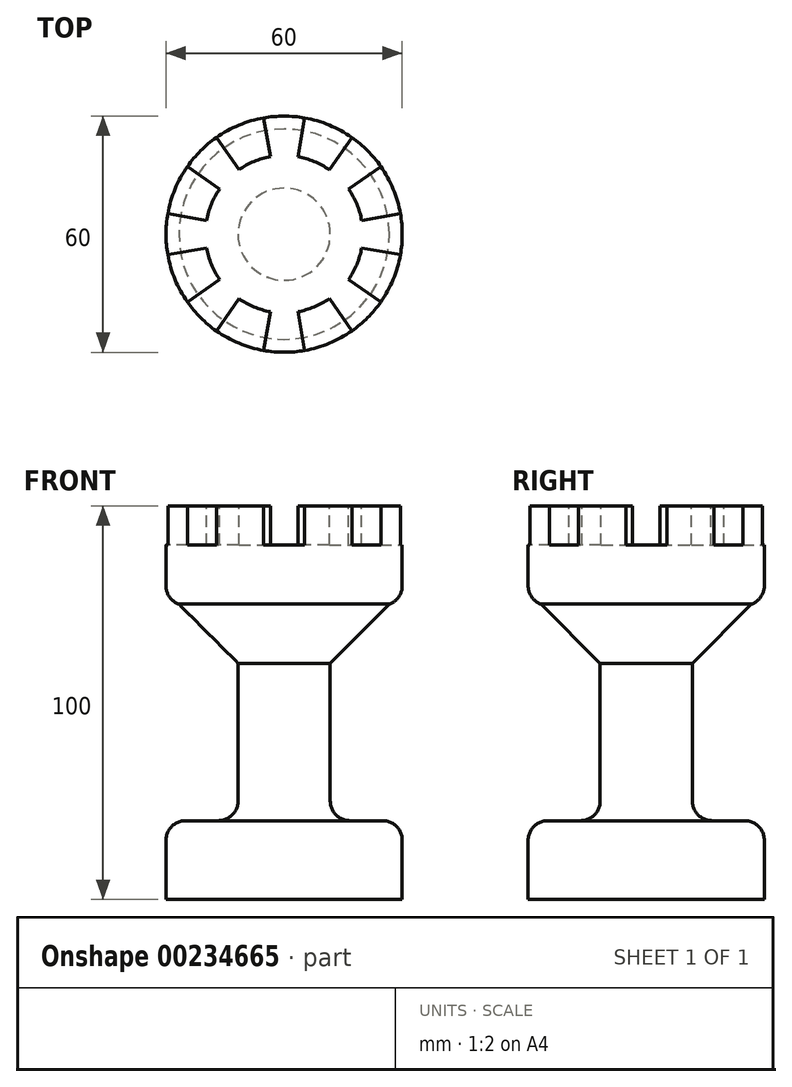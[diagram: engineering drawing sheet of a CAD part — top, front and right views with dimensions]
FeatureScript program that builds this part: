
annotation { "Feature Type Name" : "Feature", "Feature Type Description" : "" }
export const myFeature = defineFeature(function(context is Context, id is Id, definition is map)
    precondition{}
    {
        {
            var Q0;
            Q0=qCreatedBy(makeId("Front.planeOp"),FACE);
            var sketch = newSketch(context, id + "F0", { "sketchPlane" : qUnion([Q0])});
            skLineSegment(sketch, "E0.bottom", {"start": v(0, 0) * mm, "end": v(-30, 0) * mm});
            skLineSegment(sketch, "E0.top", {"start": v(-11.71, 20) * mm, "end": v(-30, 20) * mm});
            skLineSegment(sketch, "E0.right", {"start": v(-30, 0) * mm, "end": v(-30, 20) * mm});
            skLineSegment(sketch, "E1.left", {"start": v(-11.71, 75) * mm, "end": v(-11.71, 20) * mm});
            skLineSegment(sketch, "E2.bottom", {"start": v(-30, 100) * mm, "end": v(-20, 100) * mm});
            skLineSegment(sketch, "E2.top", {"start": v(-30, 75) * mm, "end": v(-11.71, 75) * mm});
            skLineSegment(sketch, "E2.left", {"start": v(-30, 100) * mm, "end": v(-30, 75) * mm});
            skLineSegment(sketch, "E3.top", {"start": v(-20, 90) * mm, "end": v(0, 90) * mm});
            skLineSegment(sketch, "E3.left", {"start": v(-20, 100) * mm, "end": v(-20, 90) * mm});
            skPoint(sketch, "E0.left.end.orphan", {"position": v(0, 20) * mm});
            skPoint(sketch, "E0.left.start.orphan", {"position": v(0, 10) * mm});
            skLineSegment(sketch, "E4", {"start": v(0, 90) * mm, "end": v(0, 0) * mm});
            skSolve(sketch);
        }
        {
            var Q0;
            Q0 = qSketchRegion(id + "F0", true);
            var Q1;
            Q1=sQuery(id+"F0.wireOp",EDGE,"E4");
            revolve(context, id + "F1", {"entities" : qUnion([Q0]), "axis" : qUnion([Q1]), "revolveType" : RevolveType.FULL});
        }
        {
            var Q0;
            Q0=makeQuery(id+"F1.opRevolve","SWEPT_FACE",FACE,{"disambiguationData":[OSD([sQuery(id+"F0.wireOp",EDGE,"E2.bottom")])]});
            var sketch = newSketch(context, id + "F2", { "sketchPlane" : qUnion([Q0])});
            skLineSegment(sketch, "E5", {"start": v(3.25, 18.43) * mm, "end": v(5.56, 31.52) * mm});
            skLineSegment(sketch, "E6", {"start": v(-3.25, 18.43) * mm, "end": v(-5.56, 31.52) * mm});
            skPoint(sketch, "E7.end.orphan", {"position": v(0, 37.14) * mm});
            skArc(sketch, "E8", {"start": v(3.25, 18.43) * mm, "mid": v(0, 18.71) * mm, "end": v(-3.25, 18.43) * mm});
            skArc(sketch, "E9", {"start": v(5.56, 31.52) * mm, "mid": v(0, 32) * mm, "end": v(-5.56, 31.52) * mm});
            skPoint(sketch, "E10.orphan", {"position": v(-6.55, 37.14) * mm});
            skPoint(sketch, "E11.orphan", {"position": v(6.55, 37.14) * mm});
            skLineSegment(sketch, "E12.1.0", {"start": v(-10.73, 15.33) * mm, "end": v(-18.36, 26.22) * mm});
            skLineSegment(sketch, "E12.1.1", {"start": v(-15.33, 10.73) * mm, "end": v(-26.22, 18.36) * mm});
            skArc(sketch, "E12.1.2", {"start": v(-18.36, 26.22) * mm, "mid": v(-22.63, 22.63) * mm, "end": v(-26.22, 18.36) * mm});
            skArc(sketch, "E12.1.3", {"start": v(-10.73, 15.33) * mm, "mid": v(-13.23, 13.23) * mm, "end": v(-15.33, 10.73) * mm});
            skLineSegment(sketch, "E12.2.0", {"start": v(-18.43, 3.25) * mm, "end": v(-31.52, 5.56) * mm});
            skLineSegment(sketch, "E12.2.1", {"start": v(-18.43, -3.25) * mm, "end": v(-31.52, -5.56) * mm});
            skArc(sketch, "E12.2.2", {"start": v(-31.52, 5.56) * mm, "mid": v(-32, 0) * mm, "end": v(-31.52, -5.56) * mm});
            skArc(sketch, "E12.2.3", {"start": v(-18.43, 3.25) * mm, "mid": v(-18.71, 0) * mm, "end": v(-18.43, -3.25) * mm});
            skLineSegment(sketch, "E12.3.0", {"start": v(-15.33, -10.73) * mm, "end": v(-26.22, -18.36) * mm});
            skLineSegment(sketch, "E12.3.1", {"start": v(-10.73, -15.33) * mm, "end": v(-18.36, -26.22) * mm});
            skArc(sketch, "E12.3.2", {"start": v(-26.22, -18.36) * mm, "mid": v(-22.63, -22.63) * mm, "end": v(-18.36, -26.22) * mm});
            skArc(sketch, "E12.3.3", {"start": v(-15.33, -10.73) * mm, "mid": v(-13.23, -13.23) * mm, "end": v(-10.73, -15.33) * mm});
            skLineSegment(sketch, "E12.4.0", {"start": v(-3.25, -18.43) * mm, "end": v(-5.56, -31.52) * mm});
            skLineSegment(sketch, "E12.4.1", {"start": v(3.25, -18.43) * mm, "end": v(5.56, -31.52) * mm});
            skArc(sketch, "E12.4.2", {"start": v(-5.56, -31.52) * mm, "mid": v(0, -32) * mm, "end": v(5.56, -31.52) * mm});
            skArc(sketch, "E12.4.3", {"start": v(-3.25, -18.43) * mm, "mid": v(0, -18.71) * mm, "end": v(3.25, -18.43) * mm});
            skLineSegment(sketch, "E12.5.0", {"start": v(10.73, -15.33) * mm, "end": v(18.36, -26.22) * mm});
            skLineSegment(sketch, "E12.5.1", {"start": v(15.33, -10.73) * mm, "end": v(26.22, -18.36) * mm});
            skArc(sketch, "E12.5.2", {"start": v(18.36, -26.22) * mm, "mid": v(22.63, -22.63) * mm, "end": v(26.22, -18.36) * mm});
            skArc(sketch, "E12.5.3", {"start": v(10.73, -15.33) * mm, "mid": v(13.23, -13.23) * mm, "end": v(15.33, -10.73) * mm});
            skLineSegment(sketch, "E12.6.0", {"start": v(18.43, -3.25) * mm, "end": v(31.52, -5.56) * mm});
            skLineSegment(sketch, "E12.6.1", {"start": v(18.43, 3.25) * mm, "end": v(31.52, 5.56) * mm});
            skArc(sketch, "E12.6.2", {"start": v(31.52, -5.56) * mm, "mid": v(32, 0) * mm, "end": v(31.52, 5.56) * mm});
            skArc(sketch, "E12.6.3", {"start": v(18.43, -3.25) * mm, "mid": v(18.71, 0) * mm, "end": v(18.43, 3.25) * mm});
            skLineSegment(sketch, "E12.7.0", {"start": v(15.33, 10.73) * mm, "end": v(26.22, 18.36) * mm});
            skLineSegment(sketch, "E12.7.1", {"start": v(10.73, 15.33) * mm, "end": v(18.36, 26.22) * mm});
            skArc(sketch, "E12.7.2", {"start": v(26.22, 18.36) * mm, "mid": v(22.63, 22.63) * mm, "end": v(18.36, 26.22) * mm});
            skArc(sketch, "E12.7.3", {"start": v(15.33, 10.73) * mm, "mid": v(13.23, 13.23) * mm, "end": v(10.73, 15.33) * mm});
            skSolve(sketch);
        }
        {
            var Q0;
            Q0 = qSketchRegion(id + "F2", true);
            extrude(context, id + "F3", {"entities" : qUnion([Q0]), "operationType" : NewBodyOperationType.REMOVE, "oppositeDirection" : true, "depth" : 10 * mm});
        }
        {
            var Q0;
            Q0=makeQuery(id+"F1.opRevolve","SWEPT_FACE",FACE,{"disambiguationData":[OSD([sQuery(id+"F0.wireOp",EDGE,"E0.top")])]});
            fillet(context, id + "F4", {"entities" : qUnion([Q0]), "radius" : 5 * mm, "tangentPropagation" : true, "allowEdgeOverflow" : false});
        }
        {
            var Q0;
            Q0=makeQuery(id+"F1.opRevolve","SWEPT_EDGE",EDGE,{"disambiguationData":[OSD([sQuery(id+"F0.wireOp",EDGE,"E1.left"),sQuery(id+"F0.wireOp",EDGE,"E2.top")])]});
            chamfer(context, id + "F5", {"entities" : qUnion([Q0]), "width" : 15 * mm, "tangentPropagation" : true});
        }
        {
            var Q0;
            Q0=makeQuery(id+"F1.opRevolve","SWEPT_EDGE",EDGE,{"disambiguationData":[OSD([sQuery(id+"F0.wireOp",EDGE,"E2.top"),sQuery(id+"F0.wireOp",EDGE,"E2.left")])]});
            fillet(context, id + "F6", {"entities" : qUnion([Q0]), "radius" : 5 * mm, "tangentPropagation" : true, "allowEdgeOverflow" : false});
        }
    });
